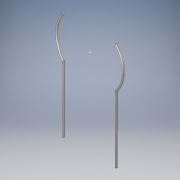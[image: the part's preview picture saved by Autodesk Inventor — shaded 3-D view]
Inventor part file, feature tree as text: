
AUTODESK INVENTOR PART (.ipt)
format: ipt  version: 2017 (Build 210142000, 142)  size: 130,560 bytes
history: native  units: in
note: dims shown in document units (in); Inventor stores cm internally (conversion verified against a paired STEP export)
features: sketch x8, plane x4, sweep x4
ambient origin geometry x8: Origin, YZ Plane, XZ Plane, XY Plane, X Axis, Y Axis, Z Axis, Center Point
bodies: Solid1 (feature_tree)
feature tree (16):
  sketch  "Sketch3"  dims[d3=8.013in d4=8.013in]
  sketch  "Sketch4"  dims[d5=0.25in d6=0.25in]
  sketch  "Sketch5"  dims[d7=0.0in d8=0.0in d9=0.0in d10=0.0in]
  plane  "Work Plane1"
  plane  "Work Plane2"
  sketch  "Sketch6"  dims[d11=0.25in d12=0.25in]
  plane  "Work Plane3"
  plane  "Work Plane4"
  sketch  "Sketch7"  dims[d13=0.0in d14=0.0in]
  sweep  "Sweep1"
  sweep  "Sweep2"
  sketch  "Sketch8"  dims[d15=0.0in d16=0.0in]
  sketch  "Sketch9"
  sweep  "Sweep3"
  sweep  "Sweep4"
  sketch  "Sketch10"
